# Revit family: Deca_Bica de mesa para cozinha_Deca You_1290.99
name_source: partatom
category: Plumbing Fixtures
units: mm (PartAtom-declared; Revit-internal decimal feet)

## family parameters
Cut with Voids When Loaded = No
Host = Face
Part Type = Normal
Room Calculation Point = No
Round Connector Dimension = Use Radius
Shared = No

## types (15) — shared parameters
Acompanha o Produto = -
Aprovado por = quattroD
Atendimento ao Cliente = 0800-0117073
Categoria = METAIS PARA COZINHA
Composição Anel Vedação = -
Composição Assento = -
Composição Básica = Liga de Cobre (bronze e latão),Plásticos de Engenharia,Elastômeros
Composição Componente = -
Consumo = -
Cor Interna = -
Cor Secundária = -
Cores Componente = -
Criado por = quattroD
Código Pai = 1290.99
Description = Bica de mesa para cozinha
Diâmetro Água Fria = 15 mm  [stored 0.0492126 ft]
Informações Complementares = -
Itens de Instalação = -
Linha = Deca You
Manufacturer = Deca
Norma = Não Possui
Pressão máx. funcionamento = 40 MCA
Pressão mín. Aquec. Acúmulo = -
Pressão mín. Aquec. Passagem = -
Pressão mín. funcionamento = 10 MCA
Raio Água Fria = 8 mm  [stored 0.0262467 ft]
Saída de Esgoto = -
Segmento = Banheiro Luxo
Tipo de dispositivo economizador = Não
Tipo de rosca de entrada = BSP NBR 8133
Tipo de rosca de saída = -
URL = www.deca.com.br
Vazão na Pressão máx. (L/min) = 16
Vazão na Pressão mín. (L/min) = 4
zero-valued in all types: Default Elevation

## per-type parameters (varying)
| type | Combinação | Cor Principal | Material | Model | Peso Líquido (Kg) | Tipo de mecanismo utilizado |
| 1290.C99_Cromado_4992.99.03 | Deca_Acionamento monocomando de mesa para cozinha_Deca You_4992.99.03 : 4992.C99.03_Cromado | Cromado | Deca_Cromado | 1290.C99 | 1.897 | Não Possui |
| 1290.INX99_Inox_4992.99.03 | Deca_Acionamento monocomando de mesa para cozinha_Deca You_4992.99.03 : 4992.INX99.03_Inox | Inox | Deca_Inox | 1290.INX99 | 1.916 | Não Possui |
| 1290.CT99.MT_Corten_4992.99.03 | Deca_Acionamento monocomando de mesa para cozinha_Deca You_4992.99.03 : 4992.CT99.MT.03_Corten | Corten | Deca_Corten | 1290.CT99.MT | 1.916 | MVC -1/4 volta |
| 1290.GL99.RD_Red Gold_4992.99.03 | Deca_Acionamento monocomando de mesa para cozinha_Deca You_4992.99.03 : 4992.GL99.RD.03_Red Gold | Red Gold | Deca_Red Gold | 1290.GL99.RD | 1.916 | MVC -1/4 volta |
| 1290.BL99.MT_Black Matte_4992.99.03 | Deca_Acionamento monocomando de mesa para cozinha_Deca You_4992.99.03 : 4992.BL99.MT.03_Black Matte | Black Matte | Deca_Black Matte | 1290.BL99.MT | 1.916 | MVC -1/4 volta |
| 1290.BL99.MT_Black Matte_4992.99.01 | Deca_Acionamento monocomando de mesa para cozinha_Deca You_4992.99.01 : 4992.BL99.MT.01_Black Matte | Black Matte | Deca_Black Matte | 1290.BL99.MT | 1.916 | MVC -1/4 volta |
| 1290.C99_Cromado_4992.99.01 | Deca_Acionamento monocomando de mesa para cozinha_Deca You_4992.99.01 : 4992.C99.01_Cromado | Cromado | Deca_Cromado | 1290.C99 | 1.897 | Não Possui |
| 1290.CT99.MT_Corten_4992.99.01 | Deca_Acionamento monocomando de mesa para cozinha_Deca You_4992.99.01 : 4992.CT99.MT.01_Corten | Corten | Deca_Corten | 1290.CT99.MT | 1.916 | MVC -1/4 volta |
| 1290.GL99.RD_Red Gold_4992.99.01 | Deca_Acionamento monocomando de mesa para cozinha_Deca You_4992.99.01 : 4992.GL99.RD.01_Red Gold | Red Gold | Deca_Red Gold | 1290.GL99.RD | 1.916 | MVC -1/4 volta |
| 1290.INX99_Inox_4992.99.01 | Deca_Acionamento monocomando de mesa para cozinha_Deca You_4992.99.01 : 4992.INX99.01_Inox | Inox | Deca_Inox | 1290.INX99 | 1.916 | Não Possui |
| 1290.BL99.MT_Black Matte_4992.99.02 | Deca_Acionamento monocomando de mesa para cozinha_Deca You_4992.99.02 : 4992.BL99.MT.02_Black Matte | Black Matte | Deca_Black Matte | 1290.BL99.MT | 1.916 | MVC -1/4 volta |
| 1290.C99_Cromado_4992.99.02 | Deca_Acionamento monocomando de mesa para cozinha_Deca You_4992.99.02 : 4992.C99.02_Cromado | Cromado | Deca_Cromado | 1290.C99 | 1.897 | Não Possui |
| 1290.CT99.MT_Corten_4992.99.02 | Deca_Acionamento monocomando de mesa para cozinha_Deca You_4992.99.02 : 4992.CT99.MT.02_Corten | Corten | Deca_Corten | 1290.CT99.MT | 1.916 | MVC -1/4 volta |
| 1290.GL99.RD_Red Gold_4992.99.02 | Deca_Acionamento monocomando de mesa para cozinha_Deca You_4992.99.02 : 4992.GL99.RD.02_Red Gold | Red Gold | Deca_Red Gold | 1290.GL99.RD | 1.916 | MVC -1/4 volta |
| 1290.INX99_Inox_4992.99.02 | Deca_Acionamento monocomando de mesa para cozinha_Deca You_4992.99.02 : 4992.INX99.02_Inox | Inox | Deca_Inox | 1290.INX99 | 1.916 | Não Possui |

note: source unit labels omitted for Vazão na Pressão máx. (L/min), Vazão na Pressão mín. (L/min) — the stored unit's dimension contradicts the parameter name (converter mislabeling)

note: [stored X ft] marks values corroborated as IEEE doubles in the binary element streams (Revit-internal decimal feet)

## geometry (parser evidence)
native form markers: Sweep x7
no freeform markers — native parametric forms only
